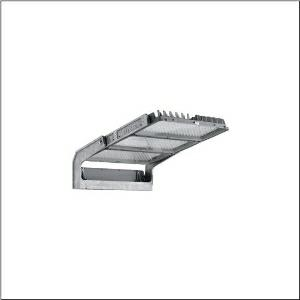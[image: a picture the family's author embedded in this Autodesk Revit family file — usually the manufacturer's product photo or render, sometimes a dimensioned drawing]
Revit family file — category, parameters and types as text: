
# Revit family: floodlight_fl_11_maxi_pro___rs07_5xa779228k01gb_83e5
name_source: partatom
category: Lighting Fixtures
units: mm (PartAtom-declared; Revit-internal decimal feet)

## family parameters
Cut with Voids When Loaded = No
Host = Face
Light Source = No
Part Type = Normal
Room Calculation Point = No
Round Connector Dimension = Use Diameter
Shared = No

## types (1)
- --- (1 x LED, 149760 lm, 1285.1 W, 5700K)
    Apparent Load = 1285 VA
    CIE Flux Codes = 80 93 99 100 99
    Color Rendering = 80
    Color Temperature = 5700K
    Default Elevation = 1800 mm
    Description = Floodlight FL 11  maxi  pro floodlight; light control with lens of PMMA; cover panel of toughened safety glass, transparent; light distribution: RS07, rotationally symmetric direct distribution, LEDcolour temperature: 5700K, rated luminous flux: 149.760lm, colour rendering: CRI > 80, light colour: 857; luminous efficacy: 117lm/W; brightness control: DMX+RDM; with terminal, 5-pole, max. 2.5mm², mains connection: 220..240V/380..400V AC, 50/60Hz, surge voltage resistance: line to ground: 10kV, service life up to 100,000h L90. Typical operating time: 1000h per year, ECG replaceable separately, LED unit replaceable without ESD environment, dustproof LED module, dimming range 10..100%; 1285W floodlight with 3x LED unit of diecast aluminium, coated grey; length: 1.003mm / width: 651mm / height: 338mm; mounting bracket, of diecast aluminium, uncoated, natural, protection rating (complete): IP66; insulation class (complete): insulation class I (protective earthing); certification: CE, ENEC, VDE; ball protection: ball impact resistant, only for outdoor installations in the designated locations, permissible operating ambient temperature: -45..+55°C, permissible storage temperature: -40..+85°Cpackaging unit: 1 piece

Light Distribution: RS07
    Height = 320 mm
    Lamp = 1 x LED
    Lamp Light Flux = 149760 lm
    Lamp Power = 1285.1 W
    Lamp count = 1
    Length = 1002 mm
    Luminous efficacy = 117 lm/W
    Manufacturer = Siteco
    ModVariant = No
    Model = 5XA779228K01GB
    Mounting Place = Ceiling
    Mounting Type = Surface mounted
    Number of Poles = 1
    OnlyDefault = Yes
    Power Factor = 1
    Product Name = Floodlight FL 11 maxi pro | RS07
    Product group = floodlight | ceiling mounted
    ProductGroupID = 301
    Protection Class = Protection class I
    Protection Degree = IP 66
    RLX_Detail_Level = 1
    RLX_Emergency_Light_Flux = 0 lm
    RLX_Emergency_Type = 0
    RLX_Emergency_Type_DB = No
    RlxData = <blob elided: 40389 chars, md5=9006491b>
    Socket = socket
    Standby Power = 0 W
    System Light Flux = 149760 lm
    System Power = 1285 W
    Type Comments = factory setting: luminous flux: 100 % | dim-lin: 255 | 875 mA
    Type Image = l_1356210.jpg
    URL = http://relux.com
    VarID = @adj_013923
    Voltage = 0 V
    Weight = 0.00 kg
    Width = 655 mm

## geometry (parser evidence)
native form markers: Blend x4, Sweep x12
no freeform markers — native parametric forms only
